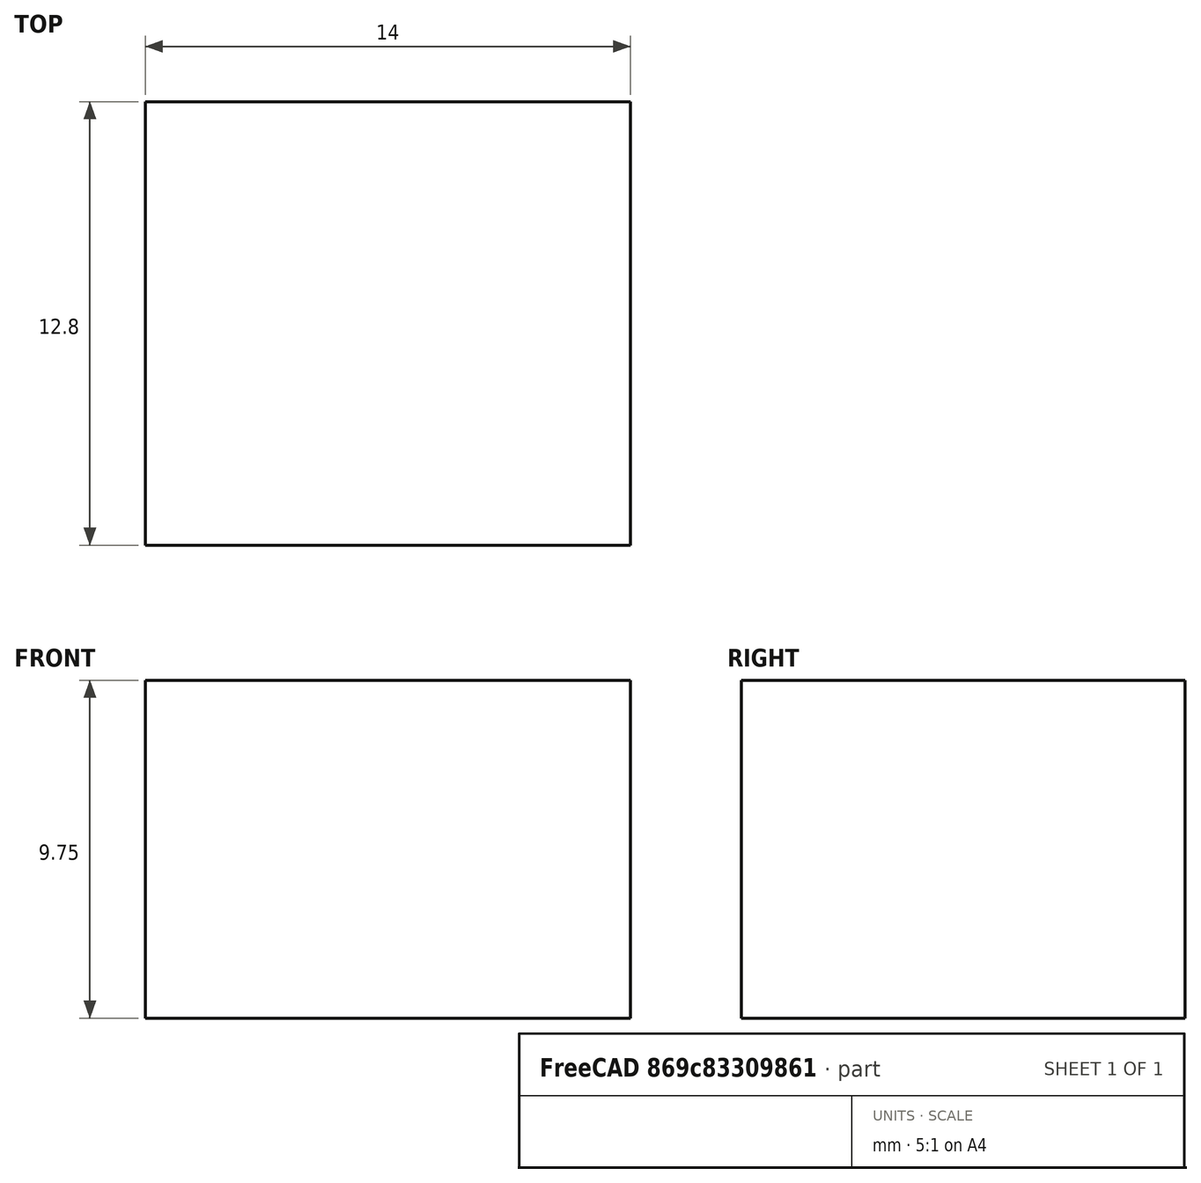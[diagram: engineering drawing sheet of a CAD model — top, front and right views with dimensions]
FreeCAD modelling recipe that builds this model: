
FCSTD DOCUMENT  (FreeCAD 1.0R39319 (Git))
Label: Molex Jr
License: All rights reserved
LicenseURL: https://en.wikipedia.org/wiki/All_rights_reserved
objects: Sketcher::SketchObject×1, PartDesign::Pad×1, PartDesign::Body×1
note: 6 computed .brp shape members not serialized (recipe doc carries the construction recipe); baked Part::Feature solids carry a one-line shape summary decoded from their .brp

FEATURE [Sketcher::SketchObject] Sketch
  ArcFitTolerance = 1e-06
  AttachmentSupport = -> [XZ_Plane]
  FullyConstrained = true
  MakeInternals = false
  MapMode = 5
  Placement = pos=(0,0,0) rot=(1,0,0;1.5708rad)
  sketch-geometry (4):
    g0: LineSegment StartX=-7 StartY=0 StartZ=0 EndX=7 EndY=0 EndZ=0
    g1: LineSegment StartX=7 StartY=0 StartZ=0 EndX=7 EndY=9.75 EndZ=0
    g2: LineSegment StartX=7 StartY=9.75 StartZ=0 EndX=-7 EndY=9.75 EndZ=0
    g3: LineSegment StartX=-7 StartY=9.75 StartZ=0 EndX=-7 EndY=0 EndZ=0
  constraints (11):
    c: Coincident(g0,g1)
    c: Coincident(g1,g2)
    c: Coincident(g2,g3)
    c: Coincident(g3,g0)
    c: Horizontal(g0)
    c: Vertical(g1)
    c: Vertical(g3)
    c: PointOnObject(g0,g-1)
    c: Symmetric(g1,g2,g-2)
    c: DistanceY(g3,g3) = 9.75
    c: DistanceX(g2,g2) = 14
FEATURE [PartDesign::Pad] Pad
  Direction = (0,-1,2e-16)
  Length = 12.8
  Length2 = 10
  Midplane = true
  Placement = pos=(0,0,0) rot=(1,0,0;1.5708rad)
  Profile = -> Sketch
  ReferenceAxis = -> Sketch [N_Axis]
  Refine = true
  Suppressed = false
  Type = 0
FEATURE [PartDesign::Body] Body
  AllowCompound = false
  Group = -> [Sketch,Pad]
  Origin = -> Origin
  Tip = -> Pad
